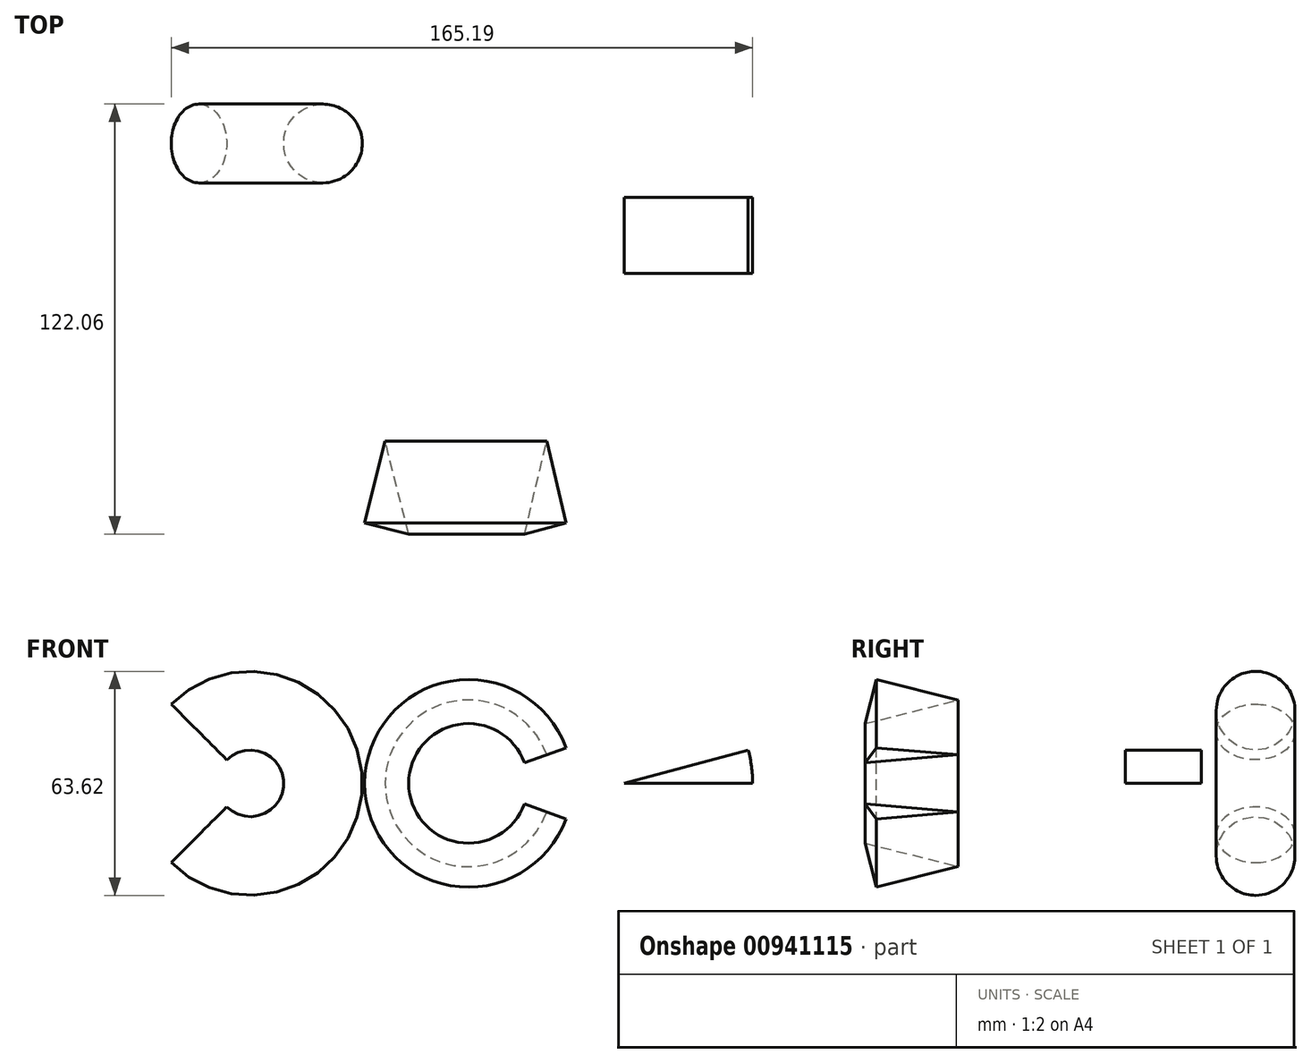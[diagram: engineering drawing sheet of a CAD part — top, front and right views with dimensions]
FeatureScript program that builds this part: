
annotation { "Feature Type Name" : "Feature", "Feature Type Description" : "" }
export const myFeature = defineFeature(function(context is Context, id is Id, definition is map)
    precondition{}
    {
        {
            var Q0;
            Q0=qCreatedBy(makeId("Top.planeOp"),FACE);
            var sketch = newSketch(context, id + "F0", { "sketchPlane" : qUnion([Q0])});
            skCircle(sketch, "E0", {"center": v(-62.28, 52.52) * mm, "radius": 11.18 * mm});
            skLineSegment(sketch, "E1.bottom", {"start": v(23.25, 37.16) * mm, "end": v(59.79, 37.16) * mm});
            skLineSegment(sketch, "E1.top", {"start": v(23.25, 15.57) * mm, "end": v(59.79, 15.57) * mm});
            skLineSegment(sketch, "E1.left", {"start": v(23.25, 37.16) * mm, "end": v(23.25, 15.57) * mm});
            skLineSegment(sketch, "E1.right", {"start": v(59.79, 37.16) * mm, "end": v(59.79, 15.57) * mm});
            skLineSegment(sketch, "E2", {"start": v(-55, -17.45) * mm, "end": v(-20.95, -29.08) * mm});
            skLineSegment(sketch, "E3", {"start": v(-20.95, -29.08) * mm, "end": v(-20.95, -63.13) * mm});
            skLineSegment(sketch, "E4", {"start": v(-20.95, -63.13) * mm, "end": v(-59.98, -69.35) * mm});
            skLineSegment(sketch, "E5", {"start": v(-59.98, -69.35) * mm, "end": v(-55, -17.45) * mm});
            skLineSegment(sketch, "E6", {"start": v(-44.62, -31.99) * mm, "end": v(-50.43, -55.24) * mm});
            skLineSegment(sketch, "E7", {"start": v(-50.43, -55.24) * mm, "end": v(-37.93, -58.36) * mm});
            skLineSegment(sketch, "E8", {"start": v(-37.93, -58.36) * mm, "end": v(-44.62, -31.99) * mm});
            skLineSegment(sketch, "E9", {"start": v(-82.91, 71.7) * mm, "end": v(-82.91, 30.26) * mm, "construction": true});
            skSolve(sketch);
        }
        {
            var Q0;
            Q0=makeQuery(id+"F0.imprint","IMPRINT",FACE,{"disambiguationData":[TD([[makeQuery(id+"F0.imprint","IMPRINT",EDGE,{"derivedFrom":sQuery(id+"F0.wireOp",EDGE,"E1.bottom")}),-1.0]])]});
            var Q1;
            Q1=sQuery(id+"F0.wireOp",EDGE,"E1.left");
            revolve(context, id + "F1", {"surfaceOperationType" : NewSurfaceOperationType.NEW, "entities" : qUnion([Q0]), "axis" : qUnion([Q1]), "revolveType" : RevolveType.ONE_DIRECTION, "angle" : 15 * degree});
        }
        {
            var Q0;
            Q0=makeQuery(id+"F0.imprint","IMPRINT",FACE,{"disambiguationData":[TD([[makeQuery(id+"F0.imprint","IMPRINT",EDGE,{"derivedFrom":sQuery(id+"F0.wireOp",EDGE,"E0")}),1.0]])]});
            var Q1;
            Q1=sQuery(id+"F0.wireOp",EDGE,"E9");
            revolve(context, id + "F2", {"surfaceOperationType" : NewSurfaceOperationType.NEW, "entities" : qUnion([Q0]), "axis" : qUnion([Q1]), "revolveType" : RevolveType.SYMMETRIC, "angle" : 270 * degree});
        }
        {
            var Q0;
            Q0=makeQuery(id+"F0.imprint","IMPRINT",FACE,{"disambiguationData":[TD([[makeQuery(id+"F0.imprint","IMPRINT",EDGE,{"derivedFrom":sQuery(id+"F0.wireOp",EDGE,"E6")}),1.0]])]});
            var Q1;
            Q1=sQuery(id+"F0.wireOp",EDGE,"E3");
            revolve(context, id + "F3", {"surfaceOperationType" : NewSurfaceOperationType.NEW, "entities" : qUnion([Q0]), "axis" : qUnion([Q1]), "revolveType" : RevolveType.SYMMETRIC, "angle" : 320 * degree});
        }
    });
